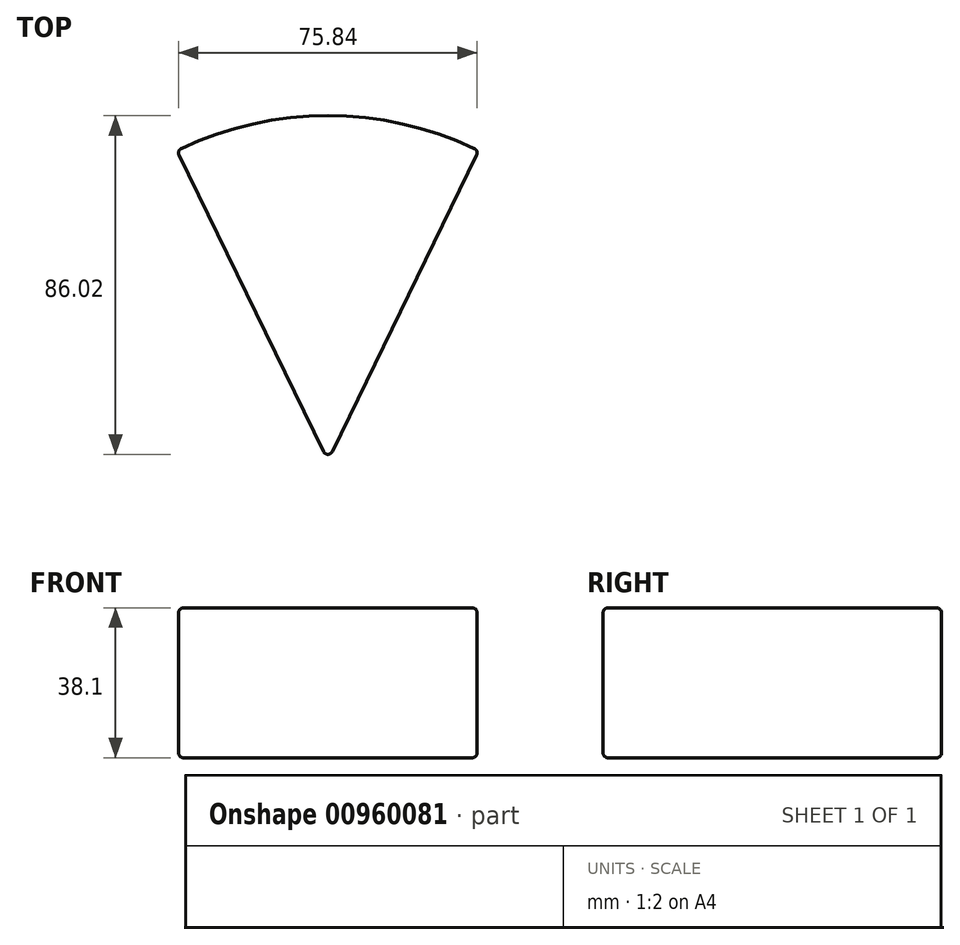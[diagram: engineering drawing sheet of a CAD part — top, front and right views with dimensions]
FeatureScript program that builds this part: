
annotation { "Feature Type Name" : "Feature", "Feature Type Description" : "" }
export const myFeature = defineFeature(function(context is Context, id is Id, definition is map)
    precondition{}
    {
        {
            var Q0;
            Q0=qCreatedBy(makeId("Top.planeOp"),FACE);
            var sketch = newSketch(context, id + "F0", { "sketchPlane" : qUnion([Q0])});
            skLineSegment(sketch, "E0", {"start": v(0, -55.8) * mm, "end": v(-38.36, 23.02) * mm});
            skLineSegment(sketch, "E1", {"start": v(0, 50.99) * mm, "end": v(0, -71.14) * mm, "construction": true});
            skLineSegment(sketch, "E2.MirrorCS", {"start": v(0, -55.8) * mm, "end": v(38.36, 23.02) * mm});
            skArc(sketch, "E3", {"start": v(-38.36, 23.02) * mm, "mid": v(0, 31.86) * mm, "end": v(38.36, 23.02) * mm});
            skSolve(sketch);
        }
        {
            var Q0;
            Q0=makeQuery(id+"F0.imprint","IMPRINT",FACE,{"disambiguationData":[TD([[makeQuery(id+"F0.imprint","IMPRINT",EDGE,{"derivedFrom":sQuery(id+"F0.wireOp",EDGE,"E0")}),-1.0]])]});
            extrude(context, id + "F1", {"entities" : qUnion([Q0]), "endBound" : BoundingType.SYMMETRIC, "depth" : 38.1 * mm, "offsetDistance" : 25.4 * mm});
        }
        {
            var Q0;
            Q0=makeQuery(id+"F1.opExtrude","CAP_FACE",FACE,{"disambiguationData":[OSD([sQuery(id+"F0.wireOp",EDGE,"E0"),sQuery(id+"F0.wireOp",EDGE,"E2.MirrorCS"),sQuery(id+"F0.wireOp",EDGE,"E3")])],"isStart":false});
            var Q1;
            Q1=makeQuery(id+"F1.opExtrude","CAP_FACE",FACE,{"disambiguationData":[OSD([sQuery(id+"F0.wireOp",EDGE,"E0"),sQuery(id+"F0.wireOp",EDGE,"E2.MirrorCS"),sQuery(id+"F0.wireOp",EDGE,"E3")])],"isStart":true});
            fillet(context, id + "F2", {"entities" : qUnion([Q0, Q1]), "radius" : 1.27 * mm, "tangentPropagation" : true, "allowEdgeOverflow" : false});
        }
        {
            var Q0;
            Q0=makeQuery(id+"F1.opExtrude","SWEPT_EDGE",EDGE,{"disambiguationData":[OSD([sQuery(id+"F0.wireOp",EDGE,"E0"),sQuery(id+"F0.wireOp",EDGE,"E2.MirrorCS")])]});
            var Q1;
            Q1=makeQuery(id+"F1.opExtrude","SWEPT_EDGE",EDGE,{"disambiguationData":[OSD([sQuery(id+"F0.wireOp",EDGE,"E2.MirrorCS"),sQuery(id+"F0.wireOp",EDGE,"E3")])]});
            var Q2;
            Q2=makeQuery(id+"F1.opExtrude","SWEPT_EDGE",EDGE,{"disambiguationData":[OSD([sQuery(id+"F0.wireOp",EDGE,"E0"),sQuery(id+"F0.wireOp",EDGE,"E3")])]});
            fillet(context, id + "F3", {"entities" : qUnion([Q0, Q1, Q2]), "radius" : 1.27 * mm, "tangentPropagation" : true, "allowEdgeOverflow" : false});
        }
    });
